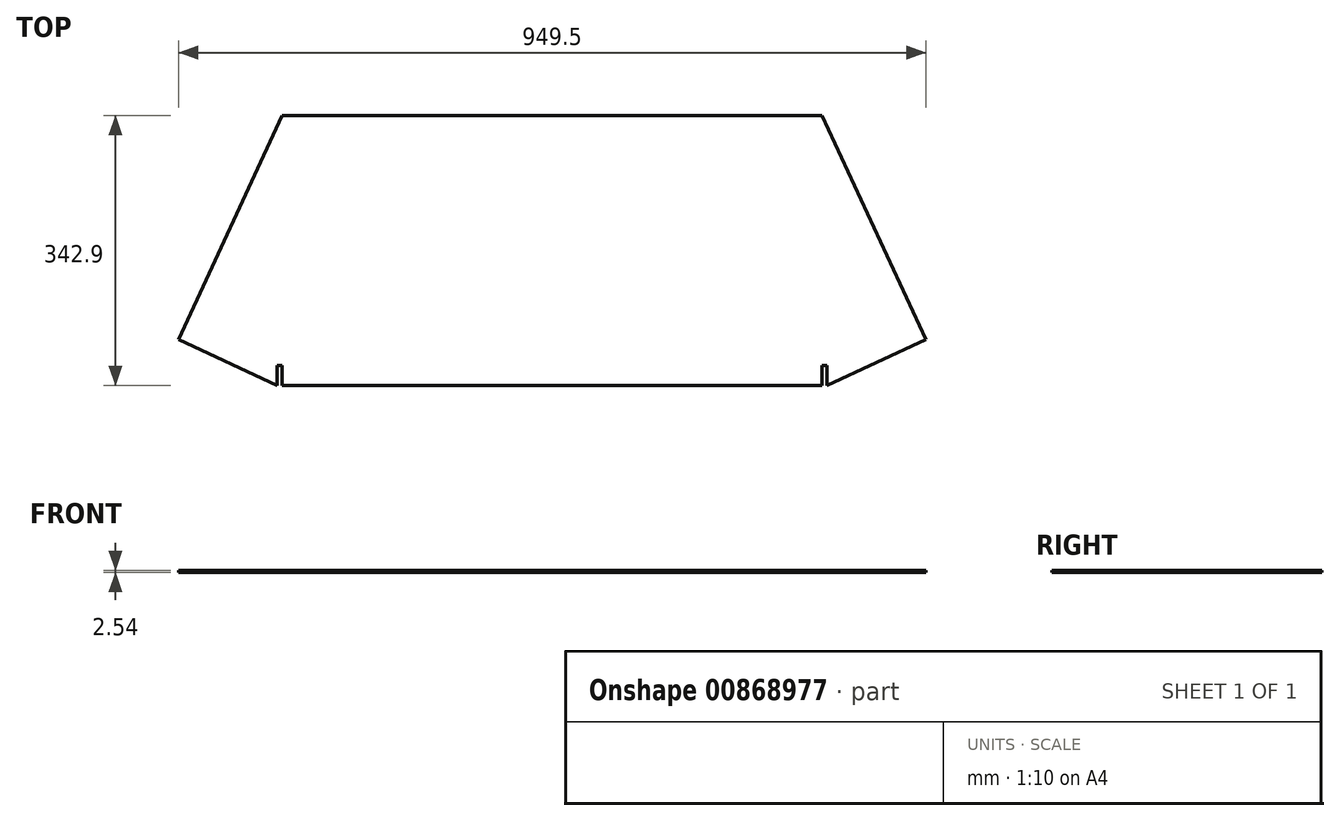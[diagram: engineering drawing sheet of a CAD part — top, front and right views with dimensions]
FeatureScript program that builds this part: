
annotation { "Feature Type Name" : "Feature", "Feature Type Description" : "" }
export const myFeature = defineFeature(function(context is Context, id is Id, definition is map)
    precondition{}
    {
        {
            var Q0;
            Q0=qCreatedBy(makeId("Top.planeOp"),FACE);
            var sketch = newSketch(context, id + "F0", { "sketchPlane" : qUnion([Q0])});
            skLineSegment(sketch, "E0", {"start": v(0, 0) * mm, "end": v(685.8, 0) * mm});
            skLineSegment(sketch, "E1", {"start": v(685.8, 0) * mm, "end": v(685.8, 25.4) * mm});
            skLineSegment(sketch, "E2", {"start": v(844.55, 0) * mm, "end": v(685.8, 342.9) * mm});
            skLineSegment(sketch, "E3", {"start": v(685.8, 342.9) * mm, "end": v(0, 342.9) * mm});
            skLineSegment(sketch, "E4", {"start": v(0, 342.9) * mm, "end": v(-158.75, 0) * mm});
            skLineSegment(sketch, "E5", {"start": v(0, 25.4) * mm, "end": v(0, 0) * mm});
            skLineSegment(sketch, "E6", {"start": v(685.8, 25.4) * mm, "end": v(692.15, 25.4) * mm});
            skLineSegment(sketch, "E7", {"start": v(692.15, 25.4) * mm, "end": v(692.15, 0) * mm});
            skLineSegment(sketch, "E8", {"start": v(692.15, 0) * mm, "end": v(844.55, 0) * mm});
            skLineSegment(sketch, "E9", {"start": v(0, 25.4) * mm, "end": v(-6.35, 25.4) * mm});
            skLineSegment(sketch, "E10", {"start": v(-6.35, 25.4) * mm, "end": v(-6.35, 0) * mm});
            skLineSegment(sketch, "E11", {"start": v(-6.35, 0) * mm, "end": v(-158.75, 0) * mm});
            skLineSegment(sketch, "E12", {"start": v(-6.35, 0) * mm, "end": v(-131.85, 58.1) * mm});
            skLineSegment(sketch, "E13", {"start": v(692.15, 0) * mm, "end": v(817.65, 58.1) * mm});
            skSolve(sketch);
        }
        {
            var Q0;
            Q0=makeQuery(id+"F0.imprint","IMPRINT",FACE,{"disambiguationData":[TD([[makeQuery(id+"F0.imprint","IMPRINT",EDGE,{"derivedFrom":sQuery(id+"F0.wireOp",EDGE,"E0")}),1.0]])]});
            extrude(context, id + "F1", {"entities" : qUnion([Q0]), "depth" : 2.54 * mm, "offsetDistance" : 25.4 * mm});
        }
    });
